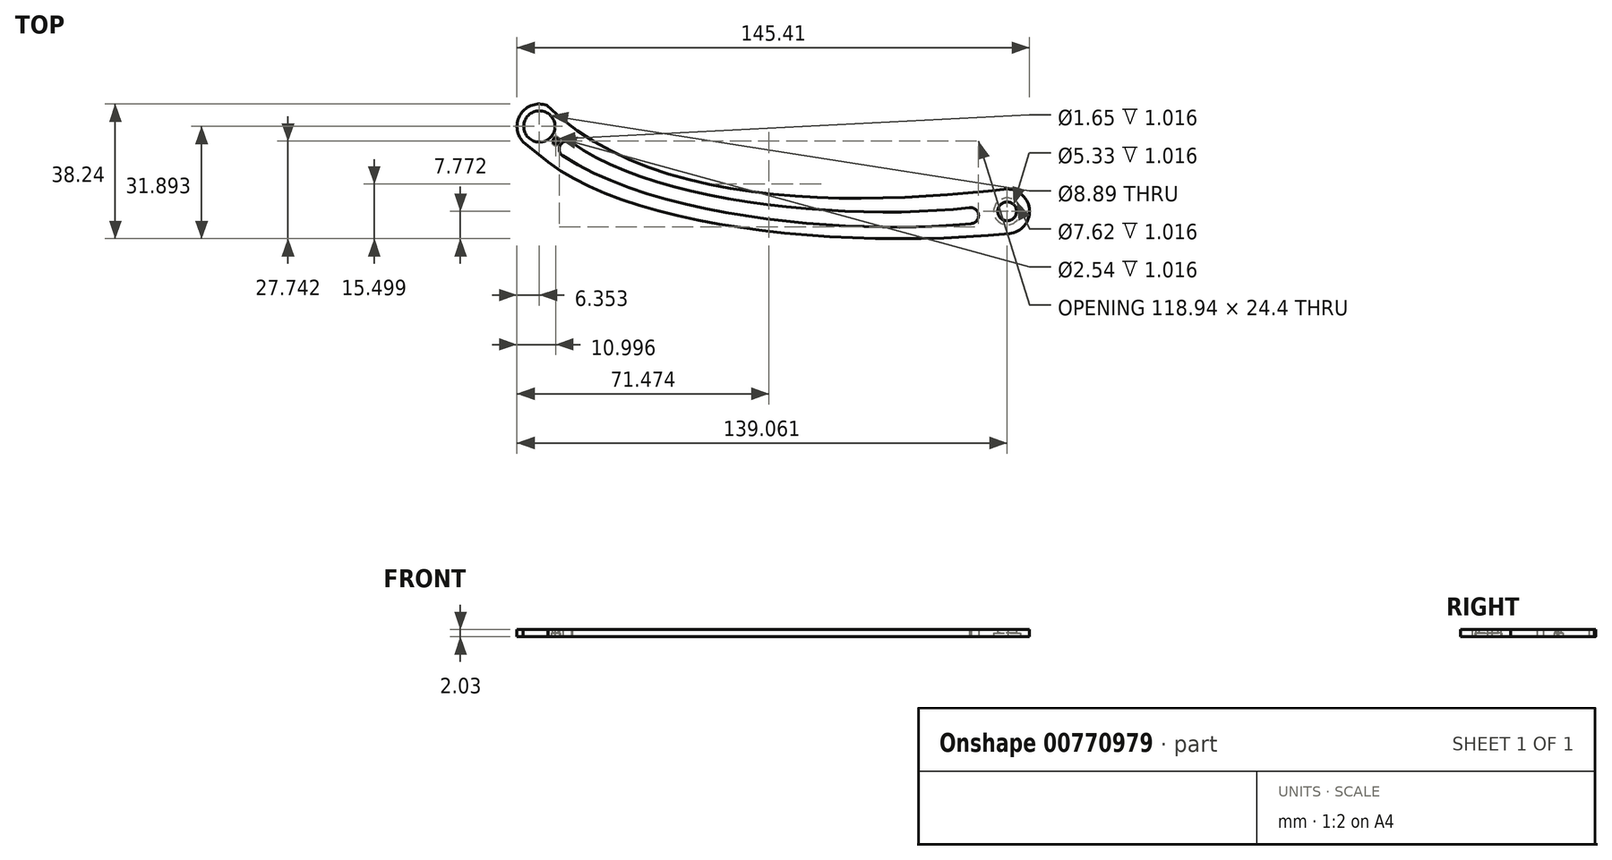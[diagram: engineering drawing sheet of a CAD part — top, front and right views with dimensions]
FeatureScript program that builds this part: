
annotation { "Feature Type Name" : "Feature", "Feature Type Description" : "" }
export const myFeature = defineFeature(function(context is Context, id is Id, definition is map)
    precondition{}
    {
        {
            var Q0;
            Q0=qCreatedBy(makeId("Top.planeOp"),FACE);
            var sketch = newSketch(context, id + "F0", { "sketchPlane" : qUnion([Q0])});
            skArc(sketch, "E0", {"start": v(-15, -65.15) * mm, "mid": v(-9.32, -58.57) * mm, "end": v(-15.52, -52.49) * mm});
            skArc(sketch, "E1", {"start": v(-146.22, -28.74) * mm, "mid": v(-153.68, -31.23) * mm, "end": v(-153, -39.07) * mm});
            skFitSpline(sketch, "E2", {"points": [v(-146.22, -28.74) * mm, v(-15.52, -52.49) * mm], "startDerivative": vector(92.44, -90.26) * mm, "endDerivative": vector(125.95, 14.09) * mm});
            skFitSpline(sketch, "E3", {"points": [v(-150.76, -40.6) * mm, v(-15, -65.15) * mm], "startDerivative": vector(65.25, -67.65) * mm, "endDerivative": vector(148.54, 14.43) * mm});
            skLineSegment(sketch, "E4", {"start": v(-153, -39.07) * mm, "end": v(-145.87, -44.9) * mm});
            skCircle(sketch, "E5", {"center": v(-148.38, -34.72) * mm, "radius": 4.45 * mm});
            skCircle(sketch, "E6", {"center": v(-15.67, -58.84) * mm, "radius": 2.67 * mm});
            skArc(sketch, "E7", {"start": v(-139.03, -39.4) * mm, "mid": v(-139.15, -39.3) * mm, "end": v(-139.27, -39.2) * mm});
            skArc(sketch, "E8", {"start": v(-25.87, -62.31) * mm, "mid": v(-23.78, -59.76) * mm, "end": v(-26.41, -57.78) * mm});
            skFitSpline(sketch, "E9", {"points": [v(-139.27, -39.2) * mm, v(-26.24, -57.75) * mm], "startDerivative": vector(69.49, -51.74) * mm, "endDerivative": vector(101.38, 12.17) * mm});
            skFitSpline(sketch, "E10", {"points": [v(-25.87, -62.31) * mm, v(-141.74, -43.12) * mm], "startDerivative": vector(-72.87, -8.27) * mm, "endDerivative": vector(-94.2, 60.5) * mm});
            skArc(sketch, "E11", {"start": v(-139.27, -39.2) * mm, "mid": v(-142.4, -39.97) * mm, "end": v(-141.74, -43.12) * mm});
            skSolve(sketch);
        }
        {
            var Q0;
            {var subQ10=sQuery(id+"F0.wireOp",EDGE,"E0");Q0=makeQuery(id+"F0.imprint","IMPRINT",FACE,{"disambiguationData":[TD([[makeQuery(id+"F0.imprint","IMPRINT",EDGE,{"derivedFrom":subQ10}),1.0]])]});}
            extrude(context, id + "F1", {"entities" : qUnion([Q0]), "depth" : 2.03 * mm, "offsetDistance" : 25.4 * mm});
        }
        {
            var Q0;
            Q0=makeQuery(id+"F1.opExtrude","CAP_FACE",FACE,{"disambiguationData":[OSD([sQuery(id+"F0.wireOp",EDGE,"E0"),sQuery(id+"F0.wireOp",EDGE,"E1"),sQuery(id+"F0.wireOp",EDGE,"E2"),sQuery(id+"F0.wireOp",EDGE,"E3"),sQuery(id+"F0.wireOp",EDGE,"E4"),sQuery(id+"F0.wireOp",EDGE,"E5"),sQuery(id+"F0.wireOp",EDGE,"E6"),sQuery(id+"F0.wireOp",EDGE,"E7"),sQuery(id+"F0.wireOp",EDGE,"E8"),sQuery(id+"F0.wireOp",EDGE,"E9"),sQuery(id+"F0.wireOp",EDGE,"E10"),sQuery(id+"F0.wireOp",EDGE,"E11")])],"isStart":false});
            var sketch = newSketch(context, id + "F2", { "sketchPlane" : qUnion([Q0])});
            skCircle(sketch, "E12", {"center": v(-15.67, -58.84) * mm, "radius": 3.81 * mm});
            skSolve(sketch);
        }
        {
            var Q0;
            Q0=makeQuery(id+"F2.imprint","IMPRINT",FACE,{"disambiguationData":[TD([[makeQuery(id+"F2.imprint","IMPRINT",EDGE,{"derivedFrom":sQuery(id+"F2.wireOp",EDGE,"E12")}),1.0]])]});
            extrude(context, id + "F3", {"entities" : qUnion([Q0]), "operationType" : NewBodyOperationType.REMOVE, "oppositeDirection" : true, "depth" : 1.02 * mm, "offsetDistance" : 25.4 * mm});
        }
        {
            var Q0;
            Q0=makeQuery(id+"F1.opExtrude","CAP_FACE",FACE,{"disambiguationData":[OSD([sQuery(id+"F0.wireOp",EDGE,"E0"),sQuery(id+"F0.wireOp",EDGE,"E1"),sQuery(id+"F0.wireOp",EDGE,"E2"),sQuery(id+"F0.wireOp",EDGE,"E3"),sQuery(id+"F0.wireOp",EDGE,"E4"),sQuery(id+"F0.wireOp",EDGE,"E5"),sQuery(id+"F0.wireOp",EDGE,"E6"),sQuery(id+"F0.wireOp",EDGE,"E7"),sQuery(id+"F0.wireOp",EDGE,"E8"),sQuery(id+"F0.wireOp",EDGE,"E9"),sQuery(id+"F0.wireOp",EDGE,"E10"),sQuery(id+"F0.wireOp",EDGE,"E11")])],"isStart":false});
            var sketch = newSketch(context, id + "F4", { "sketchPlane" : qUnion([Q0])});
            skCircle(sketch, "E13", {"center": v(-143.73, -38.87) * mm, "radius": 0.83 * mm});
            skSolve(sketch);
        }
        {
            var Q0;
            Q0=makeQuery(id+"F4.imprint","IMPRINT",FACE,{"disambiguationData":[TD([[makeQuery(id+"F4.imprint","IMPRINT",EDGE,{"derivedFrom":sQuery(id+"F4.wireOp",EDGE,"E13")}),1.0]])]});
            extrude(context, id + "F5", {"entities" : qUnion([Q0]), "operationType" : NewBodyOperationType.REMOVE, "oppositeDirection" : true, "depth" : 25.4 * mm, "offsetDistance" : 25.4 * mm});
        }
        {
            var Q0;
            Q0=makeQuery(id+"F1.opExtrude","CAP_FACE",FACE,{"disambiguationData":[OSD([sQuery(id+"F0.wireOp",EDGE,"E0"),sQuery(id+"F0.wireOp",EDGE,"E1"),sQuery(id+"F0.wireOp",EDGE,"E2"),sQuery(id+"F0.wireOp",EDGE,"E3"),sQuery(id+"F0.wireOp",EDGE,"E4"),sQuery(id+"F0.wireOp",EDGE,"E5"),sQuery(id+"F0.wireOp",EDGE,"E6"),sQuery(id+"F0.wireOp",EDGE,"E7"),sQuery(id+"F0.wireOp",EDGE,"E8"),sQuery(id+"F0.wireOp",EDGE,"E9"),sQuery(id+"F0.wireOp",EDGE,"E10"),sQuery(id+"F0.wireOp",EDGE,"E11")])],"isStart":false});
            var sketch = newSketch(context, id + "F6", { "sketchPlane" : qUnion([Q0])});
            skCircle(sketch, "E14", {"center": v(-143.73, -38.87) * mm, "radius": 1.27 * mm});
            skSolve(sketch);
        }
        {
            var Q0;
            Q0=makeQuery(id+"F6.imprint","IMPRINT",FACE,{"disambiguationData":[TD([[makeQuery(id+"F6.imprint","IMPRINT",EDGE,{"derivedFrom":sQuery(id+"F6.wireOp",EDGE,"E14")}),1.0]])]});
            extrude(context, id + "F7", {"entities" : qUnion([Q0]), "operationType" : NewBodyOperationType.REMOVE, "oppositeDirection" : true, "depth" : 1.02 * mm, "offsetDistance" : 25.4 * mm});
        }
        {
            var Q0;
            Q0=makeQuery(id+"F7.boolean.opBoolean","COPY",FACE,{"derivedFrom":makeQuery(id+"F7.opExtrude","CAP_FACE",FACE,{"disambiguationData":[OSD([sQuery(id+"F4.wireOp",EDGE,"E13"),sQuery(id+"F6.wireOp",EDGE,"E14")])],"isStart":false})});
            var Q1;
            Q1=makeQuery(id+"F3.boolean.opBoolean","COPY",FACE,{"derivedFrom":makeQuery(id+"F3.opExtrude","CAP_FACE",FACE,{"disambiguationData":[OSD([sQuery(id+"F0.wireOp",EDGE,"E6"),sQuery(id+"F2.wireOp",EDGE,"E12")])],"isStart":false})});
            var Q2;
            Q2=makeQuery(id+"F1.opExtrude","CAP_FACE",FACE,{"disambiguationData":[OSD([sQuery(id+"F0.wireOp",EDGE,"E0"),sQuery(id+"F0.wireOp",EDGE,"E1"),sQuery(id+"F0.wireOp",EDGE,"E2"),sQuery(id+"F0.wireOp",EDGE,"E3"),sQuery(id+"F0.wireOp",EDGE,"E4"),sQuery(id+"F0.wireOp",EDGE,"E5"),sQuery(id+"F0.wireOp",EDGE,"E6"),sQuery(id+"F0.wireOp",EDGE,"E7"),sQuery(id+"F0.wireOp",EDGE,"E8"),sQuery(id+"F0.wireOp",EDGE,"E9"),sQuery(id+"F0.wireOp",EDGE,"E10"),sQuery(id+"F0.wireOp",EDGE,"E11")])],"isStart":false});
            extrude(context, id + "F8", {"entities" : qUnion([Q0, Q1]), "operationType" : NewBodyOperationType.ADD, "endBound" : BoundingType.UP_TO_SURFACE, "depth" : 25.4 * mm, "endBoundEntityFace" : qUnion([Q2]), "offsetDistance" : 25.4 * mm});
        }
        {
            var Q0;
            Q0=makeQuery(id+"F1.opExtrude","CAP_FACE",FACE,{"disambiguationData":[OSD([sQuery(id+"F0.wireOp",EDGE,"E0"),sQuery(id+"F0.wireOp",EDGE,"E1"),sQuery(id+"F0.wireOp",EDGE,"E2"),sQuery(id+"F0.wireOp",EDGE,"E3"),sQuery(id+"F0.wireOp",EDGE,"E4"),sQuery(id+"F0.wireOp",EDGE,"E5"),sQuery(id+"F0.wireOp",EDGE,"E6"),sQuery(id+"F0.wireOp",EDGE,"E7"),sQuery(id+"F0.wireOp",EDGE,"E8"),sQuery(id+"F0.wireOp",EDGE,"E9"),sQuery(id+"F0.wireOp",EDGE,"E10"),sQuery(id+"F0.wireOp",EDGE,"E11")])],"isStart":true});
            var sketch = newSketch(context, id + "F9", { "sketchPlane" : qUnion([Q0])});
            skCircle(sketch, "E15", {"center": v(-15.67, 58.84) * mm, "radius": 3.81 * mm});
            skCircle(sketch, "E16", {"center": v(-143.73, 38.87) * mm, "radius": 1.27 * mm});
            skSolve(sketch);
        }
        {
            var Q0;
            Q0=makeQuery(id+"F9.imprint","IMPRINT",FACE,{"disambiguationData":[TD([[makeQuery(id+"F9.imprint","IMPRINT",EDGE,{"derivedFrom":sQuery(id+"F9.wireOp",EDGE,"E16")}),1.0]])]});
            var Q1;
            Q1=makeQuery(id+"F9.imprint","IMPRINT",FACE,{"disambiguationData":[TD([[makeQuery(id+"F9.imprint","IMPRINT",EDGE,{"derivedFrom":sQuery(id+"F9.wireOp",EDGE,"E15")}),1.0]])]});
            extrude(context, id + "F10", {"entities" : qUnion([Q0, Q1]), "operationType" : NewBodyOperationType.REMOVE, "oppositeDirection" : true, "depth" : 1.02 * mm, "offsetDistance" : 25.4 * mm});
        }
    });
